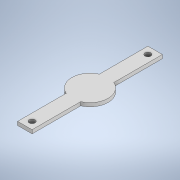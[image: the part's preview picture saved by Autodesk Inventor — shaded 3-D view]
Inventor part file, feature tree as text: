
AUTODESK INVENTOR PART (.ipt)
format: ipt  version: 2021 (Build 250183000, 183)  size: 119,808 bytes
history: native  units: mm
features: extrude x3, sketch x3, other x1, projected_geometry x1
ambient origin geometry x8: Origin, YZ Plane, XZ Plane, XY Plane, X Axis, Y Axis, Z Axis, Center Point
bodies: Body1 (feature_tree)
feature tree (8):
  other  "Sólido1"
  extrude  "Extrusión1"  Depth=180.0mm
  extrude  "Extrusión2"  Depth=5.0mm
  extrude  "Extrusión3"  Depth=10.0mm
  sketch  "Boceto1"  dims[d0=20.0mm d1=180.0mm]
  sketch  "Boceto2"  dims[d2=5.0mm d3=0.0mm d4=8.0mm]
  projected_geometry  "Contorno proyectado1"
  sketch  "Boceto3"  dims[d5=8.0mm d6=10.0mm d7=10.0mm d8=5.0mm d9=0.0mm d10=50.0mm d11=5.0mm d12=0.0mm]
